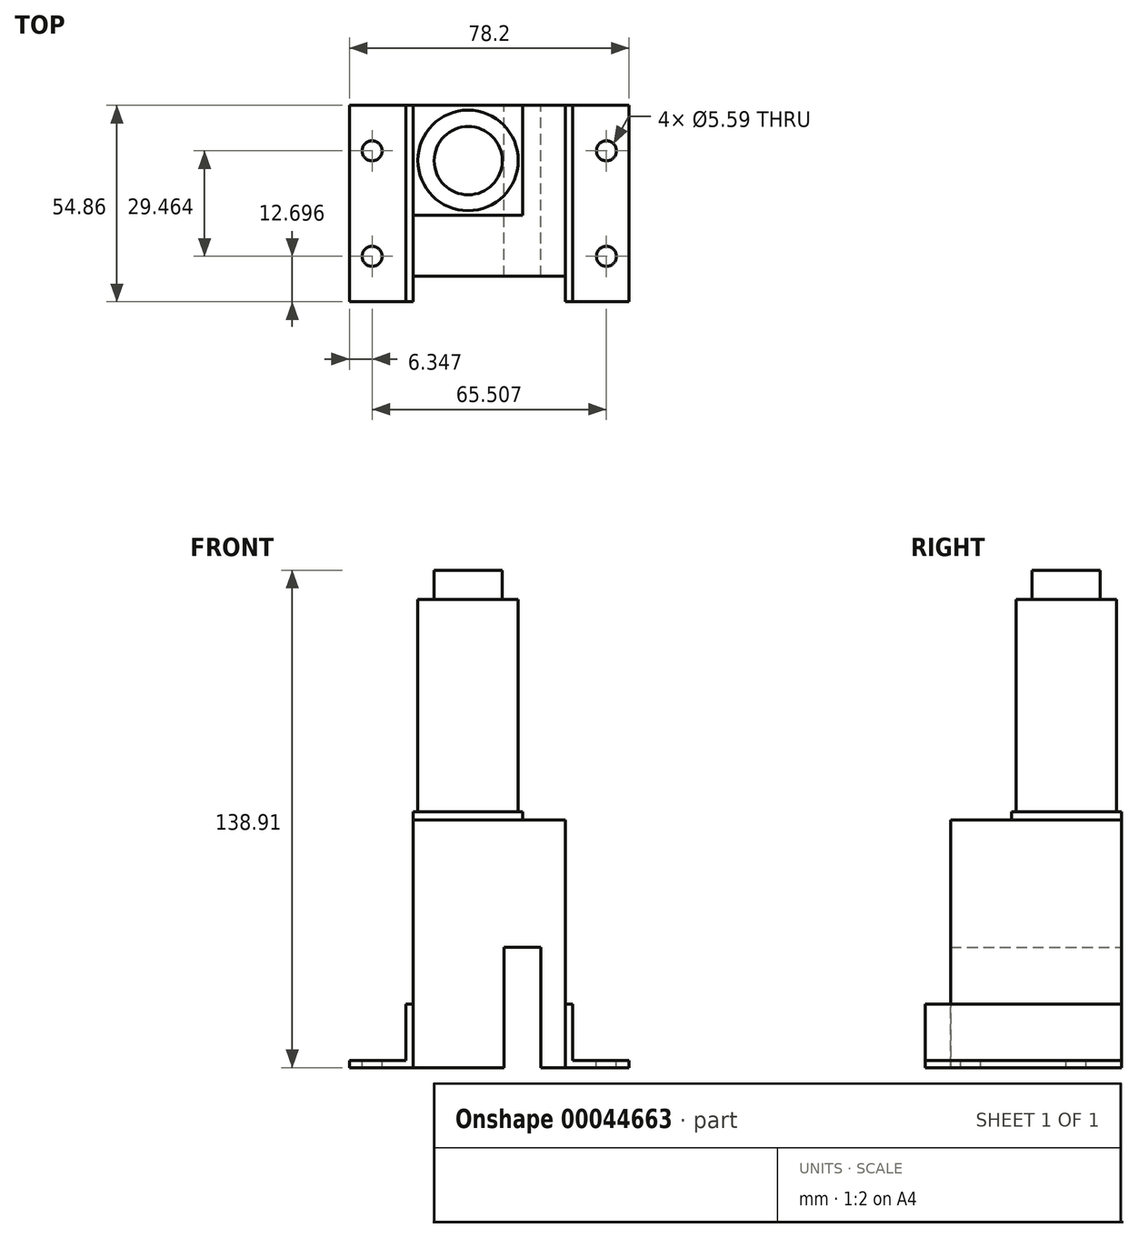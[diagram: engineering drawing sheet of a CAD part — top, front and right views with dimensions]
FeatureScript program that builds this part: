
annotation { "Feature Type Name" : "Feature", "Feature Type Description" : "" }
export const myFeature = defineFeature(function(context is Context, id is Id, definition is map)
    precondition{}
    {
        {
            var Q0;
            Q0=qCreatedBy(makeId("Front.planeOp"),FACE);
            var sketch = newSketch(context, id + "F0", { "sketchPlane" : qUnion([Q0])});
            skLineSegment(sketch, "E0", {"start": v(-21.32, 34.6) * mm, "end": v(21.32, 34.6) * mm});
            skLineSegment(sketch, "E1", {"start": v(21.32, 34.6) * mm, "end": v(21.32, -34.6) * mm});
            skLineSegment(sketch, "E2", {"start": v(21.32, -34.6) * mm, "end": v(14.39, -34.6) * mm});
            skLineSegment(sketch, "E3", {"start": v(14.39, -34.6) * mm, "end": v(14.39, -0.96) * mm});
            skLineSegment(sketch, "E4", {"start": v(14.39, -0.96) * mm, "end": v(4.08, -0.96) * mm});
            skLineSegment(sketch, "E5", {"start": v(4.08, -0.96) * mm, "end": v(4.08, -34.6) * mm});
            skLineSegment(sketch, "E6", {"start": v(4.08, -34.6) * mm, "end": v(-21.32, -34.6) * mm});
            skLineSegment(sketch, "E7", {"start": v(-21.32, -34.6) * mm, "end": v(-21.32, 34.6) * mm});
            skPoint(sketch, "E8", {"position": v(0, 0) * mm});
            skPoint(sketch, "E9.orphan", {"position": v(-21.32, 0) * mm});
            skPoint(sketch, "E10.end.orphan", {"position": v(21.32, 0) * mm});
            skSolve(sketch);
        }
        {
            var Q0;
            Q0 = qSketchRegion(id + "F0", true);
            extrude(context, id + "F1", {"entities" : qUnion([Q0]), "depth" : 47.75 * mm});
        }
        {
            var Q0;
            Q0=makeQuery(id+"F1.opExtrude","CAP_FACE",FACE,{"disambiguationData":[OSD([sQuery(id+"F0.wireOp",EDGE,"E0"),sQuery(id+"F0.wireOp",EDGE,"E1"),sQuery(id+"F0.wireOp",EDGE,"E2"),sQuery(id+"F0.wireOp",EDGE,"E3"),sQuery(id+"F0.wireOp",EDGE,"E4"),sQuery(id+"F0.wireOp",EDGE,"E5"),sQuery(id+"F0.wireOp",EDGE,"E6"),sQuery(id+"F0.wireOp",EDGE,"E7")])],"isStart":true});
            var sketch = newSketch(context, id + "F2", { "sketchPlane" : qUnion([Q0])});
            skLineSegment(sketch, "E11", {"start": v(-9.36, 34.6) * mm, "end": v(-9.36, 36.88) * mm});
            skLineSegment(sketch, "E12", {"start": v(-9.36, 36.88) * mm, "end": v(21.32, 36.88) * mm});
            skLineSegment(sketch, "E13", {"start": v(21.32, 36.88) * mm, "end": v(21.32, 34.6) * mm});
            skLineSegment(sketch, "E14", {"start": v(21.32, 34.6) * mm, "end": v(-9.36, 34.6) * mm});
            skSolve(sketch);
        }
        {
            var Q0;
            Q0 = qSketchRegion(id + "F2", true);
            extrude(context, id + "F3", {"entities" : qUnion([Q0]), "oppositeDirection" : true, "depth" : 30.68 * mm});
        }
        {
            var Q0;
            Q0=makeQuery(id+"F3.opExtrude","SWEPT_FACE",FACE,{"disambiguationData":[OSD([sQuery(id+"F2.wireOp",EDGE,"E12")])]});
            var sketch = newSketch(context, id + "F4", { "sketchPlane" : qUnion([Q0])});
            skCircle(sketch, "E15", {"center": v(-5.94, -15.38) * mm, "radius": 14.03 * mm});
            skSolve(sketch);
        }
        {
            var Q0;
            Q0 = qSketchRegion(id + "F4", true);
            extrude(context, id + "F5", {"entities" : qUnion([Q0]), "operationType" : NewBodyOperationType.ADD, "depth" : 59.3 * mm});
        }
        {
            var Q0;
            Q0=makeQuery(id+"F5.opExtrude","CAP_FACE",FACE,{"disambiguationData":[OSD([sQuery(id+"F4.wireOp",EDGE,"E15")])],"isStart":false});
            var sketch = newSketch(context, id + "F6", { "sketchPlane" : qUnion([Q0])});
            skCircle(sketch, "E16", {"center": v(-5.88, -15.44) * mm, "radius": 9.53 * mm});
            skSolve(sketch);
        }
        {
            var Q0;
            Q0 = qSketchRegion(id + "F6", true);
            extrude(context, id + "F7", {"entities" : qUnion([Q0]), "operationType" : NewBodyOperationType.ADD, "depth" : 8.13 * mm});
        }
        {
            var Q0;
            Q0=qCreatedBy(makeId("Front.planeOp"),FACE);
            var sketch = newSketch(context, id + "F8", { "sketchPlane" : qUnion([Q0])});
            skLineSegment(sketch, "E17", {"start": v(21.32, -34.6) * mm, "end": v(21.32, -16.81) * mm});
            skLineSegment(sketch, "E18", {"start": v(21.32, -16.81) * mm, "end": v(23.36, -16.81) * mm});
            skLineSegment(sketch, "E19", {"start": v(23.36, -16.81) * mm, "end": v(23.36, -32.56) * mm});
            skLineSegment(sketch, "E20", {"start": v(23.36, -32.56) * mm, "end": v(39.1, -32.56) * mm});
            skLineSegment(sketch, "E21", {"start": v(39.1, -32.56) * mm, "end": v(39.1, -34.6) * mm});
            skLineSegment(sketch, "E22", {"start": v(39.1, -34.6) * mm, "end": v(21.32, -34.6) * mm});
            skLineSegment(sketch, "E23", {"start": v(-21.32, -34.6) * mm, "end": v(-39.1, -34.6) * mm});
            skLineSegment(sketch, "E24", {"start": v(-39.1, -34.6) * mm, "end": v(-39.1, -32.56) * mm});
            skLineSegment(sketch, "E25", {"start": v(-39.1, -32.56) * mm, "end": v(-23.36, -32.56) * mm});
            skLineSegment(sketch, "E26", {"start": v(-23.36, -32.56) * mm, "end": v(-23.36, -16.81) * mm});
            skLineSegment(sketch, "E27", {"start": v(-23.36, -16.81) * mm, "end": v(-21.32, -16.81) * mm});
            skLineSegment(sketch, "E28", {"start": v(-21.32, -16.81) * mm, "end": v(-21.32, -34.6) * mm});
            skSolve(sketch);
        }
        {
            var Q0;
            Q0 = qSketchRegion(id + "F8", true);
            extrude(context, id + "F9", {"entities" : qUnion([Q0]), "operationType" : NewBodyOperationType.ADD, "depth" : 54.86 * mm});
        }
        {
            var Q0;
            Q0=makeQuery(id+"F9.opExtrude","SWEPT_FACE",FACE,{"disambiguationData":[OSD([sQuery(id+"F8.wireOp",EDGE,"E20")])]});
            var sketch = newSketch(context, id + "F10", { "sketchPlane" : qUnion([Q0])});
            skCircle(sketch, "E29", {"center": v(32.75, -42.16) * mm, "radius": 2.8 * mm});
            skCircle(sketch, "E30", {"center": v(32.75, -12.7) * mm, "radius": 2.8 * mm});
            skCircle(sketch, "E31", {"center": v(-32.75, -12.7) * mm, "radius": 2.8 * mm});
            skCircle(sketch, "E32", {"center": v(-32.75, -42.16) * mm, "radius": 2.8 * mm});
            skSolve(sketch);
        }
        {
            var Q0;
            Q0 = qSketchRegion(id + "F10", true);
            extrude(context, id + "F11", {"entities" : qUnion([Q0]), "operationType" : NewBodyOperationType.REMOVE, "oppositeDirection" : true, "depth" : 2.03 * mm});
        }
    });
